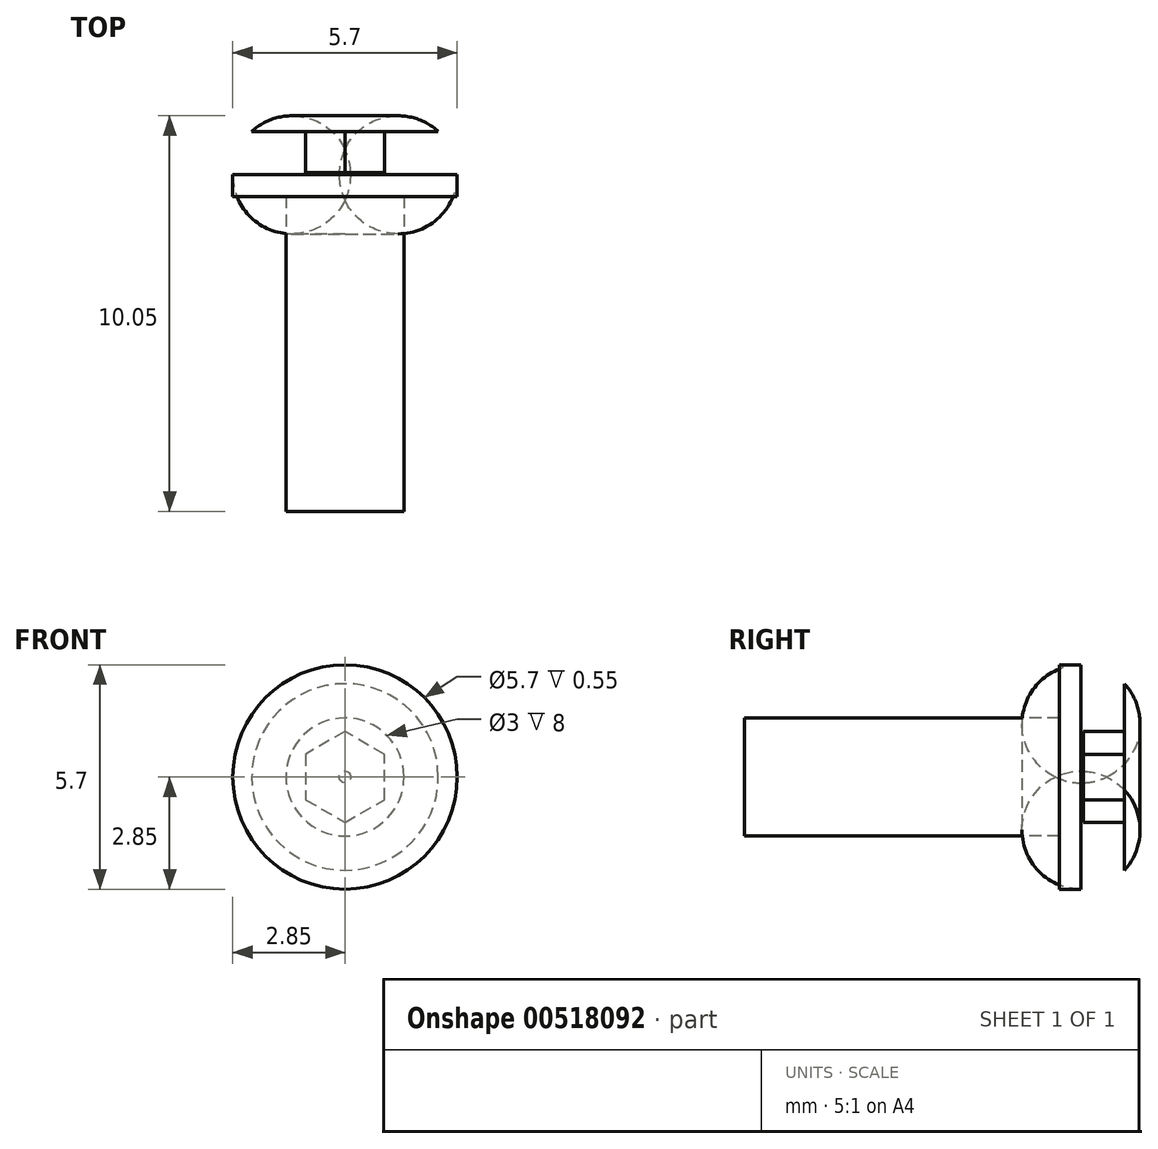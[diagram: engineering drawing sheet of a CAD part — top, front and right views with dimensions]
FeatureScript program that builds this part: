
annotation { "Feature Type Name" : "Feature", "Feature Type Description" : "" }
export const myFeature = defineFeature(function(context is Context, id is Id, definition is map)
    precondition{}
    {
        {
            assignVariable(context, id + "F0", {"name" : "t", "anyValue" : 1.04});
        }
        {
            var Q0;
            Q0=qCreatedBy(makeId("Right.planeOp"),FACE);
            var sketch = newSketch(context, id + "F1", { "sketchPlane" : qUnion([Q0])});
            skLineSegment(sketch, "E0", {"start": v(1.65, 0) * mm, "end": v(1.65, 2.37) * mm});
            skLineSegment(sketch, "E1", {"start": v(0.55, 2.85) * mm, "end": v(0, 2.85) * mm});
            skLineSegment(sketch, "E2", {"start": v(0, 2.85) * mm, "end": v(0, 1.5) * mm});
            skLineSegment(sketch, "E3", {"start": v(0, 1.5) * mm, "end": v(-8, 1.5) * mm});
            skLineSegment(sketch, "E4", {"start": v(-8, 1.5) * mm, "end": v(-8, 0) * mm});
            skLineSegment(sketch, "E5", {"start": v(-8, 0) * mm, "end": v(1.65, 0) * mm});
            skPoint(sketch, "E6.visualSharp", {"position": v(1.65, 2.85) * mm});
            skArc(sketch, "E6.filletArc", {"start": v(1.65, 2.37) * mm, "mid": v(1.15, 2.72) * mm, "end": v(0.55, 2.85) * mm});
            skSolve(sketch);
        }
        {
            var Q0;
            Q0=makeQuery(id+"F1.imprint","IMPRINT",FACE,{"disambiguationData":[TD([[makeQuery(id+"F1.imprint","IMPRINT",EDGE,{"derivedFrom":sQuery(id+"F1.wireOp",EDGE,"E0")}),1.0]])]});
            var Q1;
            Q1=sQuery(id+"F1.wireOp",EDGE,"E5");
            revolve(context, id + "F2", {"surfaceOperationType" : NewSurfaceOperationType.NEW, "entities" : qUnion([Q0]), "axis" : qUnion([Q1]), "revolveType" : RevolveType.FULL});
        }
        {
            var Q0;
            Q0=makeQuery(id+"F2.opRevolve","SWEPT_FACE",FACE,{"disambiguationData":[OSD([sQuery(id+"F1.wireOp",EDGE,"E0")])]});
            var sketch = newSketch(context, id + "F3", { "sketchPlane" : qUnion([Q0])});
            skCircle(sketch, "E7.cCircle", {"center": v(0, 0) * mm, "radius": 1 * mm, "construction": true});
            skLineSegment(sketch, "E7.0", {"start": v(-1, -0.58) * mm, "end": v(-1, 0.58) * mm});
            skLineSegment(sketch, "E7.1", {"start": v(-1, 0.58) * mm, "end": v(0, 1.15) * mm});
            skLineSegment(sketch, "E7.2", {"start": v(0, 1.15) * mm, "end": v(1, 0.58) * mm});
            skLineSegment(sketch, "E7.3", {"start": v(1, 0.58) * mm, "end": v(1, -0.58) * mm});
            skLineSegment(sketch, "E7.4", {"start": v(1, -0.58) * mm, "end": v(0, -1.15) * mm});
            skLineSegment(sketch, "E7.5", {"start": v(0, -1.15) * mm, "end": v(-1, -0.58) * mm});
            skPoint(sketch, "E7.0.midPoint", {"position": v(-1, 0) * mm});
            skSolve(sketch);
        }
        {
            var Q0;
            Q0=makeQuery(id+"F3.imprint","IMPRINT",FACE,{"disambiguationData":[TD([[makeQuery(id+"F3.imprint","IMPRINT",EDGE,{"derivedFrom":sQuery(id+"F3.wireOp",EDGE,"E7.0")}),-1.0]])]});
            extrude(context, id + "F4", {"entities" : qUnion([Q0]), "operationType" : NewBodyOperationType.REMOVE, "oppositeDirection" : true, "depth" : (getVariable(context, 't')) * mm, "offsetDistance" : 25 * mm});
        }
    });
